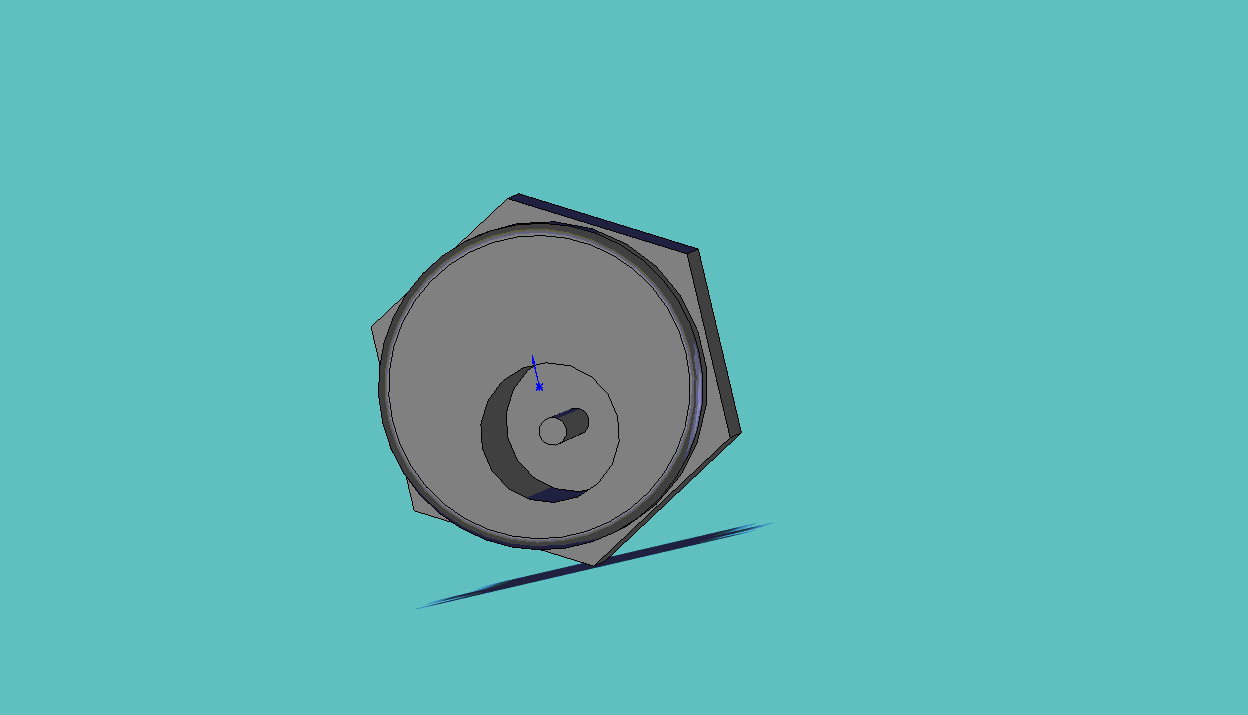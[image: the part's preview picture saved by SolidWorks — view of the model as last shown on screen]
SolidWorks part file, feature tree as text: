
SOLIDWORKS PART (.sldprt)
format: sldprt  version: not decoded by parser v0  size: 254,976 bytes
history: native  units: mm
features: sketch x5, cut_extrude x4, plane x3, material x1, revolve x1, fillet x1 (+10 scaffold rows collapsed)
feature tree (25):
  scaffold x10  (default folders/planes/origin — collapsed)
  material  "Matériau <non spécifié>"
  plane  "Plan de face"
  plane  "Plan de dessus"
  plane  "Plan de droite"
  sketch  "Esquisse1"  dims[D1=14.0mm D2=11.0mm D3=20.0mm D4=2.0mm D5=4.0mm D6=2.0mm D7=6.0mm D8=12.4mm]
  revolve  "Révolution1"  Angle=360deg
  sketch  "Esquisse2"  dims[D1=14.0mm]
  cut_extrude  "Enlèv. mat.-Extru.1"  Depth=4mm
  sketch  "Esquisse3"  dims[D2=1.2mm D3=6.0mm D1=2.0mm]
  cut_extrude  "Enlèv. mat.-Extru.2"  Depth=9mm
  sketch  "Esquisse4"
  cut_extrude  "Enlèv. mat.-Extru.3"  Depth=1mm
  sketch  "Esquisse5"  dims[D2=11.0mm D1=11.4mm]
  cut_extrude  "Enlèv. mat.-Extru.5"  Depth=2mm
  fillet  "Congé1"  Radius=0.5mm
decode coverage: 10 of 11 modeling features carry decoded parameters
note: suppression state not decoded; provenance and decode notes live in map.json
